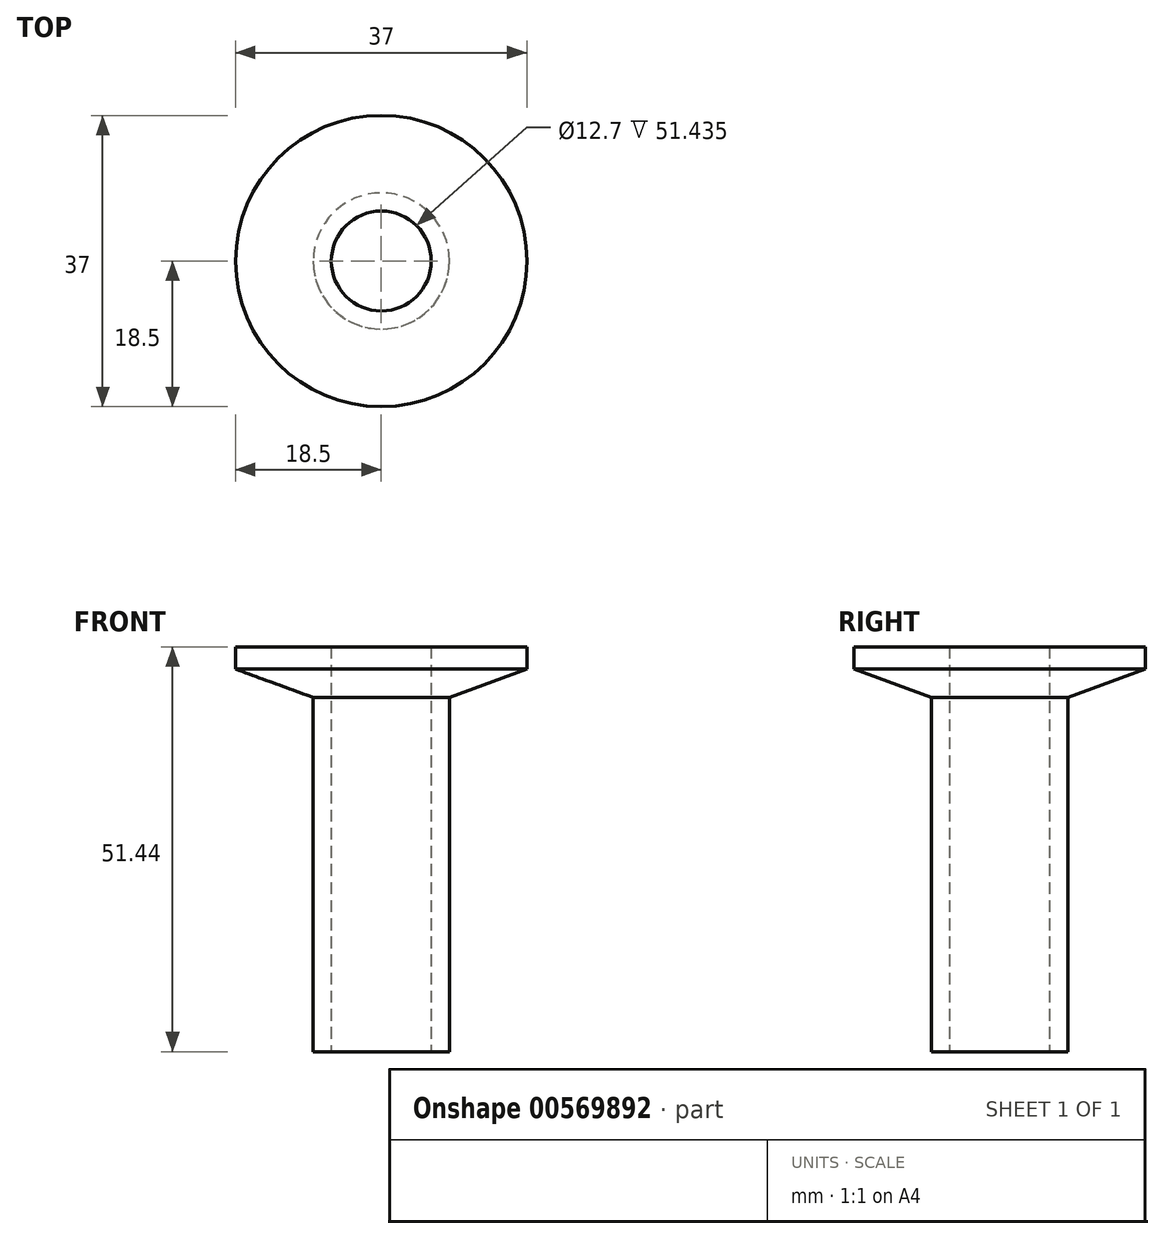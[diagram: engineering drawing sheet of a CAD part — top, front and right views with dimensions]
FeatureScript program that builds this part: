
annotation { "Feature Type Name" : "Feature", "Feature Type Description" : "" }
export const myFeature = defineFeature(function(context is Context, id is Id, definition is map)
    precondition{}
    {
        {
            var Q0;
            Q0=qCreatedBy(makeId("Front.planeOp"),FACE);
            var sketch = newSketch(context, id + "F0", { "sketchPlane" : qUnion([Q0])});
            skLineSegment(sketch, "E0", {"start": v(6.35, 0) * mm, "end": v(6.35, 6.44) * mm});
            skLineSegment(sketch, "E1", {"start": v(6.35, 6.44) * mm, "end": v(18.5, 6.44) * mm});
            skLineSegment(sketch, "E2", {"start": v(18.5, 6.44) * mm, "end": v(18.5, 3.59) * mm});
            skLineSegment(sketch, "E3", {"start": v(18.5, 3.59) * mm, "end": v(8.65, 0) * mm});
            skLineSegment(sketch, "E4", {"start": v(8.65, 0) * mm, "end": v(6.35, 0) * mm});
            skLineSegment(sketch, "E5", {"start": v(0, 0) * mm, "end": v(0, 11.29) * mm, "construction": true});
            skSolve(sketch);
        }
        {
            var Q0;
            Q0 = qSketchRegion(id + "F0", true);
            var Q1;
            Q1=sQuery(id+"F0.wireOp",EDGE,"E5");
            revolve(context, id + "F1", {"entities" : qUnion([Q0]), "axis" : qUnion([Q1]), "revolveType" : RevolveType.FULL});
        }
        {
            var Q0;
            Q0=qCreatedBy(makeId("Top.planeOp"),FACE);
            var sketch = newSketch(context, id + "F2", { "sketchPlane" : qUnion([Q0])});
            skCircle(sketch, "E6", {"center": v(0, 0) * mm, "radius": 8.65 * mm});
            skCircle(sketch, "E7", {"center": v(0, 0) * mm, "radius": 6.35 * mm});
            skSolve(sketch);
        }
        {
            var Q0;
            Q0 = qSketchRegion(id + "F2", true);
            extrude(context, id + "F3", {"entities" : qUnion([Q0]), "operationType" : NewBodyOperationType.ADD, "oppositeDirection" : true, "depth" : 45 * mm, "offsetDistance" : 25 * mm});
        }
    });
